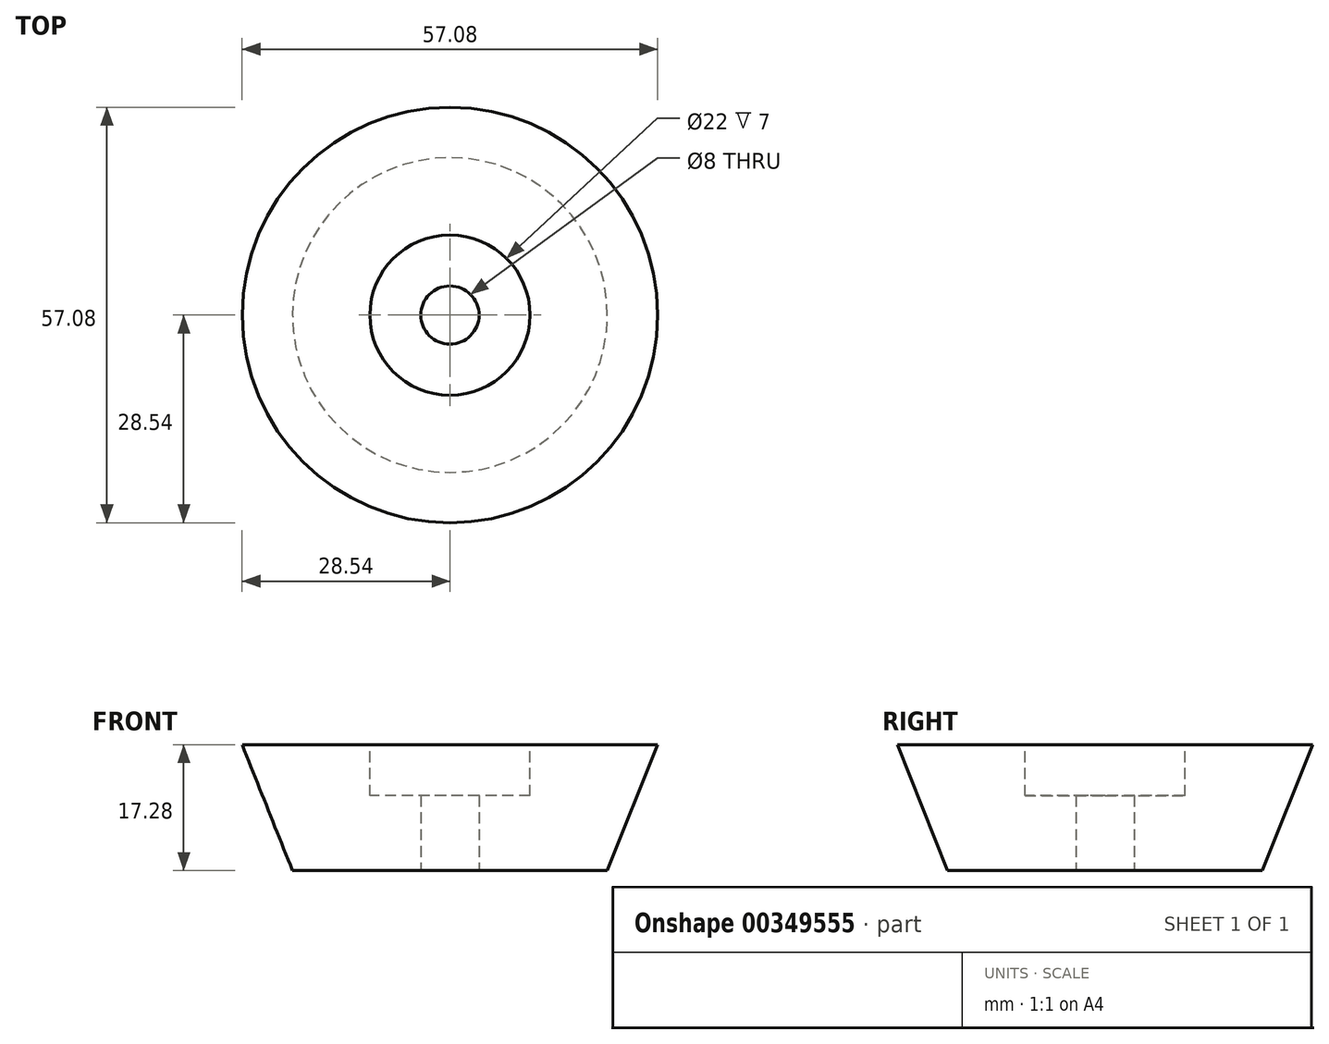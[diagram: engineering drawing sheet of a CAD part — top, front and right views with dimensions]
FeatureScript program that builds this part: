
annotation { "Feature Type Name" : "Feature", "Feature Type Description" : "" }
export const myFeature = defineFeature(function(context is Context, id is Id, definition is map)
    precondition{}
    {
        {
            var Q0;
            Q0=qCreatedBy(makeId("Front.planeOp"),FACE);
            var sketch = newSketch(context, id + "F0", { "sketchPlane" : qUnion([Q0])});
            skLineSegment(sketch, "E0", {"start": v(0, 17.27) * mm, "end": v(28.54, 17.27) * mm});
            skLineSegment(sketch, "E1", {"start": v(28.54, 17.27) * mm, "end": v(21.62, -0.01) * mm});
            skLineSegment(sketch, "E2", {"start": v(21.62, -0.01) * mm, "end": v(0, -0.01) * mm});
            skLineSegment(sketch, "E3", {"start": v(0, -0.01) * mm, "end": v(0, 17.27) * mm});
            skSolve(sketch);
        }
        {
            var Q0;
            Q0=makeQuery(id+"F0.imprint","IMPRINT",FACE,{"disambiguationData":[TD([[makeQuery(id+"F0.imprint","IMPRINT",EDGE,{"derivedFrom":sQuery(id+"F0.wireOp",EDGE,"E0")}),-1.0]])]});
            var Q1;
            Q1=sQuery(id+"F0.wireOp",EDGE,"E3");
            revolve(context, id + "F1", {"entities" : qUnion([Q0]), "axis" : qUnion([Q1]), "revolveType" : RevolveType.FULL});
        }
        {
            var Q0;
            Q0=makeQuery(id+"F1.opRevolve","SWEPT_FACE",FACE,{"disambiguationData":[OSD([sQuery(id+"F0.wireOp",EDGE,"E0")])]});
            var sketch = newSketch(context, id + "F2", { "sketchPlane" : qUnion([Q0])});
            skCircle(sketch, "E4", {"center": v(0, 0) * mm, "radius": 11 * mm});
            skSolve(sketch);
        }
        {
            var Q0;
            Q0 = qSketchRegion(id + "F2", true);
            extrude(context, id + "F3", {"entities" : qUnion([Q0]), "operationType" : NewBodyOperationType.REMOVE, "oppositeDirection" : true, "depth" : 7 * mm});
        }
        {
            var Q0;
            Q0=makeQuery(id+"F1.opRevolve","SWEPT_FACE",FACE,{"disambiguationData":[OSD([sQuery(id+"F0.wireOp",EDGE,"E2")])]});
            var sketch = newSketch(context, id + "F4", { "sketchPlane" : qUnion([Q0])});
            skCircle(sketch, "E5", {"center": v(0, 0) * mm, "radius": 4 * mm});
            skSolve(sketch);
        }
        {
            var Q0;
            Q0 = qSketchRegion(id + "F4", true);
            extrude(context, id + "F5", {"entities" : qUnion([Q0]), "operationType" : NewBodyOperationType.REMOVE, "oppositeDirection" : true, "depth" : 25 * mm});
        }
    });
